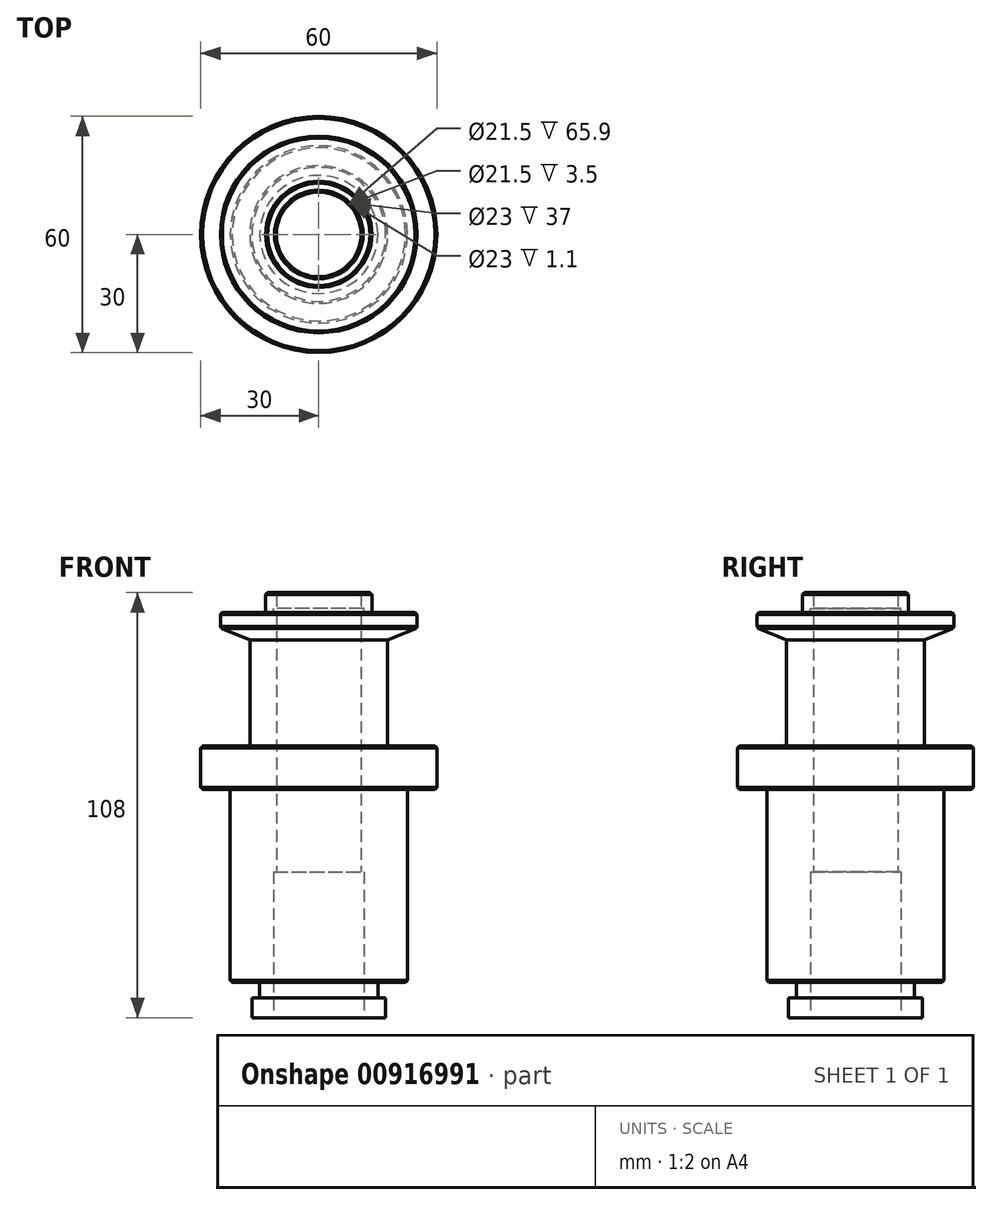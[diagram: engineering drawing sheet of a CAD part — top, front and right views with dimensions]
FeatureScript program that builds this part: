
annotation { "Feature Type Name" : "Feature", "Feature Type Description" : "" }
export const myFeature = defineFeature(function(context is Context, id is Id, definition is map)
    precondition{}
    {
        {
            var Q0;
            Q0=qCreatedBy(makeId("Top.planeOp"),FACE);
            var sketch = newSketch(context, id + "F0", { "sketchPlane" : qUnion([Q0])});
            skCircle(sketch, "E0", {"center": v(0, 0) * mm, "radius": 13.5 * mm});
            skCircle(sketch, "E1", {"center": v(0, 0) * mm, "radius": 10.75 * mm});
            skSolve(sketch);
        }
        {
            var Q0;
            Q0=makeQuery(id+"F0.imprint","IMPRINT",FACE,{"disambiguationData":[TD([[makeQuery(id+"F0.imprint","IMPRINT",EDGE,{"derivedFrom":sQuery(id+"F0.wireOp",EDGE,"E0")}),1.0]])]});
            extrude(context, id + "F1", {"entities" : qUnion([Q0]), "depth" : 5 * mm, "offsetDistance" : 25 * mm});
        }
        {
            var Q0;
            Q0=makeQuery(id+"F1.opExtrude","CAP_FACE",FACE,{"disambiguationData":[OSD([sQuery(id+"F0.wireOp",EDGE,"E0"),sQuery(id+"F0.wireOp",EDGE,"E1")])],"isStart":true});
            var sketch = newSketch(context, id + "F2", { "sketchPlane" : qUnion([Q0])});
            skCircle(sketch, "E2", {"center": v(0, 0) * mm, "radius": 25 * mm});
            skSolve(sketch);
        }
        {
            var Q0;
            Q0=makeQuery(id+"F2.imprint","IMPRINT",FACE,{"disambiguationData":[TD([[makeQuery(id+"F2.imprint","IMPRINT",EDGE,{"derivedFrom":makeQuery(id+"F1.opExtrude","CAP_EDGE",EDGE,{"disambiguationData":[OSD([sQuery(id+"F0.wireOp",EDGE,"E0")])],"isStart":true})}),-1.0]])]});
            var Q1;
            Q1=makeQuery(id+"F2.imprint","IMPRINT",FACE,{"disambiguationData":[TD([[makeQuery(id+"F2.imprint","IMPRINT",EDGE,{"derivedFrom":makeQuery(id+"F1.opExtrude","CAP_EDGE",EDGE,{"disambiguationData":[OSD([sQuery(id+"F0.wireOp",EDGE,"E1")])],"isStart":true})}),-1.0]])]});
            var Q2;
            Q2=makeQuery(id+"F2.imprint","IMPRINT",FACE,{"disambiguationData":[TD([[makeQuery(id+"F2.imprint","IMPRINT",EDGE,{"derivedFrom":sQuery(id+"F2.wireOp",EDGE,"E2")}),1.0]])]});
            extrude(context, id + "F3", {"entities" : qUnion([Q0, Q1, Q2]), "operationType" : NewBodyOperationType.ADD, "depth" : 7 * mm, "offsetDistance" : 25 * mm});
        }
        {
            var Q0;
            Q0=makeQuery(id+"F3.opExtrude","CAP_FACE",FACE,{"disambiguationData":[OSD([sQuery(id+"F2.wireOp",EDGE,"E2")])],"isStart":false});
            var sketch = newSketch(context, id + "F4", { "sketchPlane" : qUnion([Q0])});
            skCircle(sketch, "E3", {"center": v(0, 0) * mm, "radius": 17.5 * mm});
            skSolve(sketch);
        }
        {
            var Q0;
            Q0=qSketchRegion(id+"F4",true);
            extrude(context, id + "F5", {"entities" : qUnion([Q0]), "operationType" : NewBodyOperationType.ADD, "depth" : 27 * mm, "offsetDistance" : 25 * mm});
        }
        {
            var Q0;
            Q0=makeQuery(id+"F5.opExtrude","CAP_FACE",FACE,{"disambiguationData":[OSD([sQuery(id+"F4.wireOp",EDGE,"E3")])],"isStart":false});
            var sketch = newSketch(context, id + "F6", { "sketchPlane" : qUnion([Q0])});
            skCircle(sketch, "E4", {"center": v(0, 0) * mm, "radius": 30 * mm});
            skSolve(sketch);
        }
        {
            var Q0;
            Q0=makeQuery(id+"F6.imprint","IMPRINT",FACE,{"disambiguationData":[TD([[makeQuery(id+"F6.imprint","IMPRINT",EDGE,{"derivedFrom":makeQuery(id+"F5.opExtrude","CAP_EDGE",EDGE,{"disambiguationData":[OSD([sQuery(id+"F4.wireOp",EDGE,"E3")])],"isStart":false})}),1.0]])]});
            var Q1;
            Q1=makeQuery(id+"F6.imprint","IMPRINT",FACE,{"disambiguationData":[TD([[makeQuery(id+"F6.imprint","IMPRINT",EDGE,{"derivedFrom":sQuery(id+"F6.wireOp",EDGE,"E4")}),1.0]])]});
            extrude(context, id + "F7", {"entities" : qUnion([Q0, Q1]), "operationType" : NewBodyOperationType.ADD, "depth" : 11 * mm, "offsetDistance" : 25 * mm});
        }
        {
            var Q0;
            Q0=makeQuery(id+"F7.opExtrude","CAP_FACE",FACE,{"disambiguationData":[OSD([sQuery(id+"F6.wireOp",EDGE,"E4")])],"isStart":false});
            var sketch = newSketch(context, id + "F8", { "sketchPlane" : qUnion([Q0])});
            skCircle(sketch, "E5", {"center": v(0, 0) * mm, "radius": 22.5 * mm});
            skSolve(sketch);
        }
        {
            var Q0;
            Q0=makeQuery(id+"F8.imprint","IMPRINT",FACE,{"disambiguationData":[TD([[makeQuery(id+"F8.imprint","IMPRINT",EDGE,{"derivedFrom":sQuery(id+"F8.wireOp",EDGE,"E5")}),1.0]])]});
            extrude(context, id + "F9", {"entities" : qUnion([Q0]), "operationType" : NewBodyOperationType.ADD, "depth" : 49 * mm, "offsetDistance" : 25 * mm});
        }
        {
            var Q0;
            Q0=makeQuery(id+"F9.opExtrude","CAP_FACE",FACE,{"disambiguationData":[OSD([sQuery(id+"F8.wireOp",EDGE,"E5")])],"isStart":false});
            var sketch = newSketch(context, id + "F10", { "sketchPlane" : qUnion([Q0])});
            skCircle(sketch, "E6", {"center": v(0, 0) * mm, "radius": 15 * mm});
            skSolve(sketch);
        }
        {
            var Q0;
            Q0=makeQuery(id+"F10.imprint","IMPRINT",FACE,{"disambiguationData":[TD([[makeQuery(id+"F10.imprint","IMPRINT",EDGE,{"derivedFrom":sQuery(id+"F10.wireOp",EDGE,"E6")}),1.0]])]});
            extrude(context, id + "F11", {"entities" : qUnion([Q0]), "operationType" : NewBodyOperationType.ADD, "depth" : 4 * mm, "offsetDistance" : 25 * mm});
        }
        {
            var Q0;
            Q0=makeQuery(id+"F11.opExtrude","CAP_FACE",FACE,{"disambiguationData":[OSD([sQuery(id+"F10.wireOp",EDGE,"E6")])],"isStart":false});
            var sketch = newSketch(context, id + "F12", { "sketchPlane" : qUnion([Q0])});
            skCircle(sketch, "E7", {"center": v(0, 0) * mm, "radius": 17 * mm});
            skSolve(sketch);
        }
        {
            var Q0;
            Q0=makeQuery(id+"F12.imprint","IMPRINT",FACE,{"disambiguationData":[TD([[makeQuery(id+"F12.imprint","IMPRINT",EDGE,{"derivedFrom":sQuery(id+"F12.wireOp",EDGE,"E7")}),1.0]])]});
            var Q1;
            Q1=makeQuery(id+"F12.imprint","IMPRINT",FACE,{"disambiguationData":[TD([[makeQuery(id+"F12.imprint","IMPRINT",EDGE,{"derivedFrom":makeQuery(id+"F11.opExtrude","CAP_EDGE",EDGE,{"disambiguationData":[OSD([sQuery(id+"F10.wireOp",EDGE,"E6")])],"isStart":false})}),1.0]])]});
            extrude(context, id + "F13", {"entities" : qUnion([Q0, Q1]), "operationType" : NewBodyOperationType.ADD, "depth" : 5 * mm, "offsetDistance" : 25 * mm});
        }
        {
            var Q0;
            Q0=makeQuery(id+"F13.opExtrude","CAP_FACE",FACE,{"disambiguationData":[OSD([sQuery(id+"F12.wireOp",EDGE,"E7")])],"isStart":false});
            var sketch = newSketch(context, id + "F14", { "sketchPlane" : qUnion([Q0])});
            skCircle(sketch, "E8", {"center": v(0, 0) * mm, "radius": 11.5 * mm});
            skSolve(sketch);
        }
        {
            var Q0;
            Q0=makeQuery(id+"F14.imprint","IMPRINT",FACE,{"disambiguationData":[TD([[makeQuery(id+"F14.imprint","IMPRINT",EDGE,{"derivedFrom":sQuery(id+"F14.wireOp",EDGE,"E8")}),1.0]])]});
            extrude(context, id + "F15", {"entities" : qUnion([Q0]), "operationType" : NewBodyOperationType.REMOVE, "oppositeDirection" : true, "depth" : 37 * mm, "offsetDistance" : 25 * mm});
        }
        {
            var Q0;
            Q0=makeQuery(id+"F3.boolean.opBoolean","SPLIT",FACE,{"disambiguationData":[TD([makeQuery(id+"F1.opExtrude","SWEPT_FACE",FACE,{"disambiguationData":[OSD([sQuery(id+"F0.wireOp",EDGE,"E1")])]})])],"derivedFrom":makeQuery(id+"F3.opExtrude","CAP_FACE",FACE,{"disambiguationData":[OSD([sQuery(id+"F2.wireOp",EDGE,"E2")])],"isStart":true})});
            var sketch = newSketch(context, id + "F16", { "sketchPlane" : qUnion([Q0])});
            skCircle(sketch, "E9", {"center": v(0, 0) * mm, "radius": 10.75 * mm});
            skSolve(sketch);
        }
        {
            var Q0;
            Q0=makeQuery(id+"F16.imprint","IMPRINT",FACE,{"disambiguationData":[TD([[makeQuery(id+"F16.imprint","IMPRINT",EDGE,{"derivedFrom":sQuery(id+"F16.wireOp",EDGE,"E9")}),1.0]])]});
            extrude(context, id + "F17", {"entities" : qUnion([Q0]), "operationType" : NewBodyOperationType.REMOVE, "endBound" : BoundingType.THROUGH_ALL, "oppositeDirection" : true, "depth" : 25 * mm, "offsetDistance" : 25 * mm});
        }
        {
            var Q0;
            Q0=makeQuery(id+"F15.boolean.opBoolean","COPY",EDGE,{"derivedFrom":makeQuery(id+"F15.opExtrude","CAP_EDGE",EDGE,{"disambiguationData":[OSD([sQuery(id+"F14.wireOp",EDGE,"E8")])],"isStart":true})});
            var Q1;
            Q1=makeQuery(id+"F9.opExtrude","CAP_EDGE",EDGE,{"disambiguationData":[OSD([sQuery(id+"F8.wireOp",EDGE,"E5")])],"isStart":false});
            var Q2;
            Q2=makeQuery(id+"F7.opExtrude","CAP_EDGE",EDGE,{"disambiguationData":[OSD([sQuery(id+"F6.wireOp",EDGE,"E4")])],"isStart":false});
            var Q3;
            Q3=makeQuery(id+"F7.opExtrude","CAP_EDGE",EDGE,{"disambiguationData":[OSD([sQuery(id+"F6.wireOp",EDGE,"E4")])],"isStart":true});
            var Q4;
            Q4=makeQuery(id+"F3.opExtrude","CAP_EDGE",EDGE,{"disambiguationData":[OSD([sQuery(id+"F2.wireOp",EDGE,"E2")])],"isStart":true});
            var Q5;
            Q5=makeQuery(id+"F1.opExtrude","CAP_EDGE",EDGE,{"disambiguationData":[OSD([sQuery(id+"F0.wireOp",EDGE,"E0")])],"isStart":false});
            var Q6;
            Q6=makeQuery(id+"F1.opExtrude","CAP_EDGE",EDGE,{"disambiguationData":[OSD([sQuery(id+"F0.wireOp",EDGE,"E1")])],"isStart":false});
            chamfer(context, id + "F18", {"entities" : qUnion([Q0, Q1, Q2, Q3, Q4, Q5, Q6]), "width" : .5 * mm, "tangentPropagation" : true});
        }
        {
            var Q0;
            Q0=makeQuery(id+"F3.opExtrude","CAP_EDGE",EDGE,{"disambiguationData":[OSD([sQuery(id+"F2.wireOp",EDGE,"E2")])],"isStart":false});
            chamfer(context, id + "F19", {"entities" : qUnion([Q0]), "chamferType" : ChamferType.TWO_OFFSETS, "width1" : 7.5 * mm, "oppositeDirection" : false, "width2" : 3 * mm, "tangentPropagation" : true});
        }
        {
            var Q0;
            {var subQ0=sQuery(id+"F2.wireOp",EDGE,"E2");Q0=makeQuery(id+"F19.opChamfer","BLEND_EDGE",EDGE,{"blendedFrom":[makeQuery(id+"F3.opExtrude","CAP_EDGE",EDGE,{"disambiguationData":[OSD([subQ0])],"isStart":false}),makeQuery(id+"F3.opExtrude","SWEPT_FACE",FACE,{"disambiguationData":[OSD([subQ0])]})],"blendedInto":[makeQuery(id+"F3.opExtrude","SWEPT_FACE",FACE,{"disambiguationData":[OSD([subQ0])]})]});}
            chamfer(context, id + "F20", {"entities" : qUnion([Q0]), "width" : .5 * mm, "tangentPropagation" : true});
        }
        {
            var Q0;
            Q0=makeQuery(id+"F1.opExtrude","CAP_FACE",FACE,{"disambiguationData":[OSD([sQuery(id+"F0.wireOp",EDGE,"E0"),sQuery(id+"F0.wireOp",EDGE,"E1")])],"isStart":false});
            cPlane(context, id + "F21", {"entities" : qUnion([Q0]), "cplaneType" : CPlaneType.OFFSET, "offset" : 4 * mm, "oppositeDirection" : true, "width" : 150 * mm, "height" : 150 * mm});
        }
        {
            var Q0;
            Q0=qCreatedBy(id+"F21.planeOp",FACE);
            var sketch = newSketch(context, id + "F22", { "sketchPlane" : qUnion([Q0])});
            skCircle(sketch, "E10", {"center": v(0, 0) * mm, "radius": 11.5 * mm});
            skSolve(sketch);
        }
        {
            var Q0;
            Q0=makeQuery(id+"F22.imprint","IMPRINT",FACE,{"disambiguationData":[TD([[makeQuery(id+"F22.imprint","IMPRINT",EDGE,{"derivedFrom":sQuery(id+"F22.wireOp",EDGE,"E10")}),1.0]])]});
            extrude(context, id + "F23", {"entities" : qUnion([Q0]), "operationType" : NewBodyOperationType.REMOVE, "oppositeDirection" : true, "depth" : 1.1 * mm, "offsetDistance" : 25 * mm});
        }
    });
